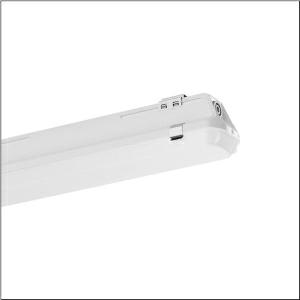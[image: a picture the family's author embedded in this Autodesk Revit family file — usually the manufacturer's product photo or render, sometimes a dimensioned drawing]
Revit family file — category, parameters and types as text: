
# Revit family: monsun_r__11_51fp10ep460h_f2a9
name_source: partatom
category: Lighting Fixtures
units: mm (PartAtom-declared; Revit-internal decimal feet)

## family parameters
Cut with Voids When Loaded = No
Host = Face
Light Source = No
Part Type = Normal
Room Calculation Point = No
Round Connector Dimension = Use Diameter
Shared = No

## types (1)
- --- (1 x LED, 6050 lm, 34.6 W, 4000K)
    Apparent Load = 35 VA
    CIE Flux Codes = 47 77 93 94 100
    Color Rendering = 80
    Color Temperature = 4000K
    Default Elevation = 1800 mm
    Description = Monsun® 11, damp-proof luminaire, chain hanger, primary optical cover: enclosure, of PMMA, light emission: direct distribution, primary light characteristic: symmetric, installation type: suspended mounting, surface-mounted, horizontal mounting, vertical mounting, LED, rated luminous flux: 6.050lm, luminous efficacy: 175lm/W, light colour: 840, colour temperature: 4000K, control gear: ECG DALI, with terminal, 5-pole, max. 2.5mm², mains connection: 220..240V, AC, 50/60Hz, rated input power: 35W, luminaire housing, of glass-fibre reinforced polyester, uncoated, bright grey, incl. chain hanger, length: 1.590mm, width: 90mm, height: 88mm, clip for enclosure, of stainless steel (V2A), ceiling mounting element, of stainless steel (V2A), chain hanger, of stainless steel (V2A), protection rating (complete): IP66, insulation class (complete): insulation class I (protective earthing), certification: CE, ENEC, VDE, UKCA, protection symbol: D, impact resistance: IK04, permissible operating ambient temperature: -25..+40°C, standard: EN 50419, EN 60598-2-1, no direct snow, no direct sun, no direct rain, for indoor or canopied outdoor use, corresponds to IFS (International Featured Standards) requirements for safety and quality in the food industry, contact your sales advisor before using the luminaires in applications with unclear chemical exposure, large temperature fluctuations or condensation-forming humidity, LABS conformity tested according to VDMA 24364:2018-05, packaging unit: 1 piece
    Height = 89 mm
    Lamp = 1 x LED
    Lamp Light Flux = 6050 lm
    Lamp Power = 34.6 W
    Lamp count = 1
    Length = 1590 mm
    Luminous efficacy = 175 lm/W
    Manufacturer = Siteco
    ModVariant = No
    Model = 51FP10EP460H
    Mounting Place = Ceiling
    Mounting Type = Surface mounted
    Number of Poles = 1
    OnlyDefault = Yes
    Power Factor = 1
    Product Name = Monsun® 11
    Product group = damp-proof luminaire
    ProductGroupID = 300
    Protection Class = Protection class I
    Protection Degree = IP 66
    RLX_Detail_Level = 1
    RLX_Emergency_Light_Flux = 0 lm
    RLX_Emergency_Type = 0
    RLX_Emergency_Type_DB = No
    RlxData = <blob elided: 92021 chars, md5=5e3b8cc6>
    Socket = socket
    Standby Power = 0 W
    System Light Flux = 6050 lm
    System Power = 35 W
    Type Comments = factory setting: luminous flux: 100 % | dim-lin: 254 | 232 mA
    Type Image = l_1004748.jpg
    URL = http://relux.com
    VarID = @adj_142267
    Voltage = 0 V
    Weight = 0.00 kg
    Width = 90 mm

## geometry (parser evidence)
native form markers: Blend x4, Sweep x13
no freeform markers — native parametric forms only
